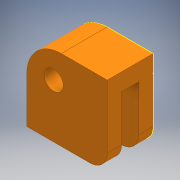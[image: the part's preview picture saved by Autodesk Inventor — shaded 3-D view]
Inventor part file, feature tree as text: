
AUTODESK INVENTOR PART (.ipt)
format: ipt  version: 2017 (Build 210142000, 142)  size: 167,424 bytes
history: native  units: mm
features: sketch x5, extrude x4, plane x1, fillet x1, projected_geometry x1
ambient origin geometry x8: Origin, YZ Plane, XZ Plane, XY Plane, X Axis, Y Axis, Z Axis, Center Point
bodies: Solid1 (feature_tree)
feature tree (12):
  extrude  "Extrusion1"  Depth=3.0mm
  extrude  "Extrusion2"  Depth=3.0mm
  plane  "Work Plane1"
  extrude  "Extrusion3"  Depth=8.0mm TaperAngle=0.0deg
  sketch  "Sketch4"  dims[d7=2.5mm d8=0.0mm d9=3.0mm d10=2.5mm d11=0.0mm]
  extrude  "Extrusion4"  Depth=3.0mm
  fillet  "Fillet2"  Radius=2.5mm
  sketch  "Sketch1"  dims[d0=3.0mm d1=3.0mm]
  sketch  "Sketch2"  dims[d2=8.0mm d3=3.0mm]
  sketch  "Sketch3"  dims[d4=8.0mm d5=8.0mm d6=0.0mm]
  projected_geometry  "Projected Loop1"
  sketch  "Sketch5"  dims[d21=3.333333mm d22=3.0mm d23=3.0mm d24=2.5mm d25=0.0mm d26=0.25mm]
